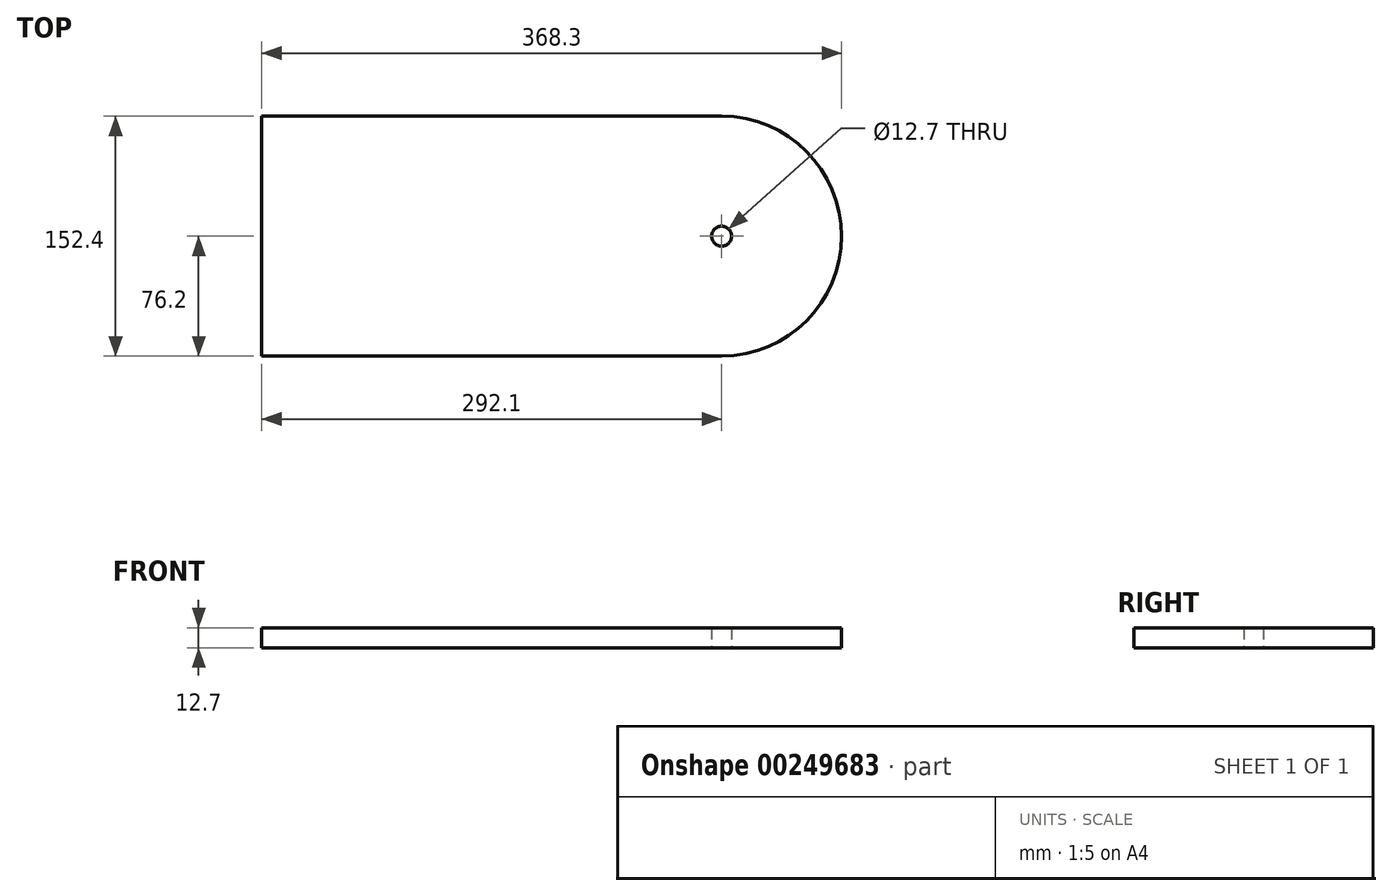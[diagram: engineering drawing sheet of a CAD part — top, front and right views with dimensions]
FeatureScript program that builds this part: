
annotation { "Feature Type Name" : "Feature", "Feature Type Description" : "" }
export const myFeature = defineFeature(function(context is Context, id is Id, definition is map)
    precondition{}
    {
        {
            var Q0;
            Q0=qCreatedBy(makeId("Top.planeOp"),FACE);
            var sketch = newSketch(context, id + "F0", { "sketchPlane" : qUnion([Q0])});
            skArc(sketch, "E0", {"start": v(0, -76.2) * mm, "mid": v(76.2, 0) * mm, "end": v(0, 76.2) * mm});
            skCircle(sketch, "E1", {"center": v(0, 0) * mm, "radius": 6.35 * mm});
            skLineSegment(sketch, "E2", {"start": v(0, 76.2) * mm, "end": v(-292.1, 76.2) * mm});
            skLineSegment(sketch, "E3", {"start": v(-292.1, 76.2) * mm, "end": v(-292.1, -76.2) * mm});
            skLineSegment(sketch, "E4", {"start": v(-292.1, -76.2) * mm, "end": v(0, -76.2) * mm});
            skSolve(sketch);
        }
        {
            var Q0;
            Q0 = qSketchRegion(id + "F0", true);
            extrude(context, id + "F1", {"entities" : qUnion([Q0]), "depth" : 12.7 * mm});
        }
    });
